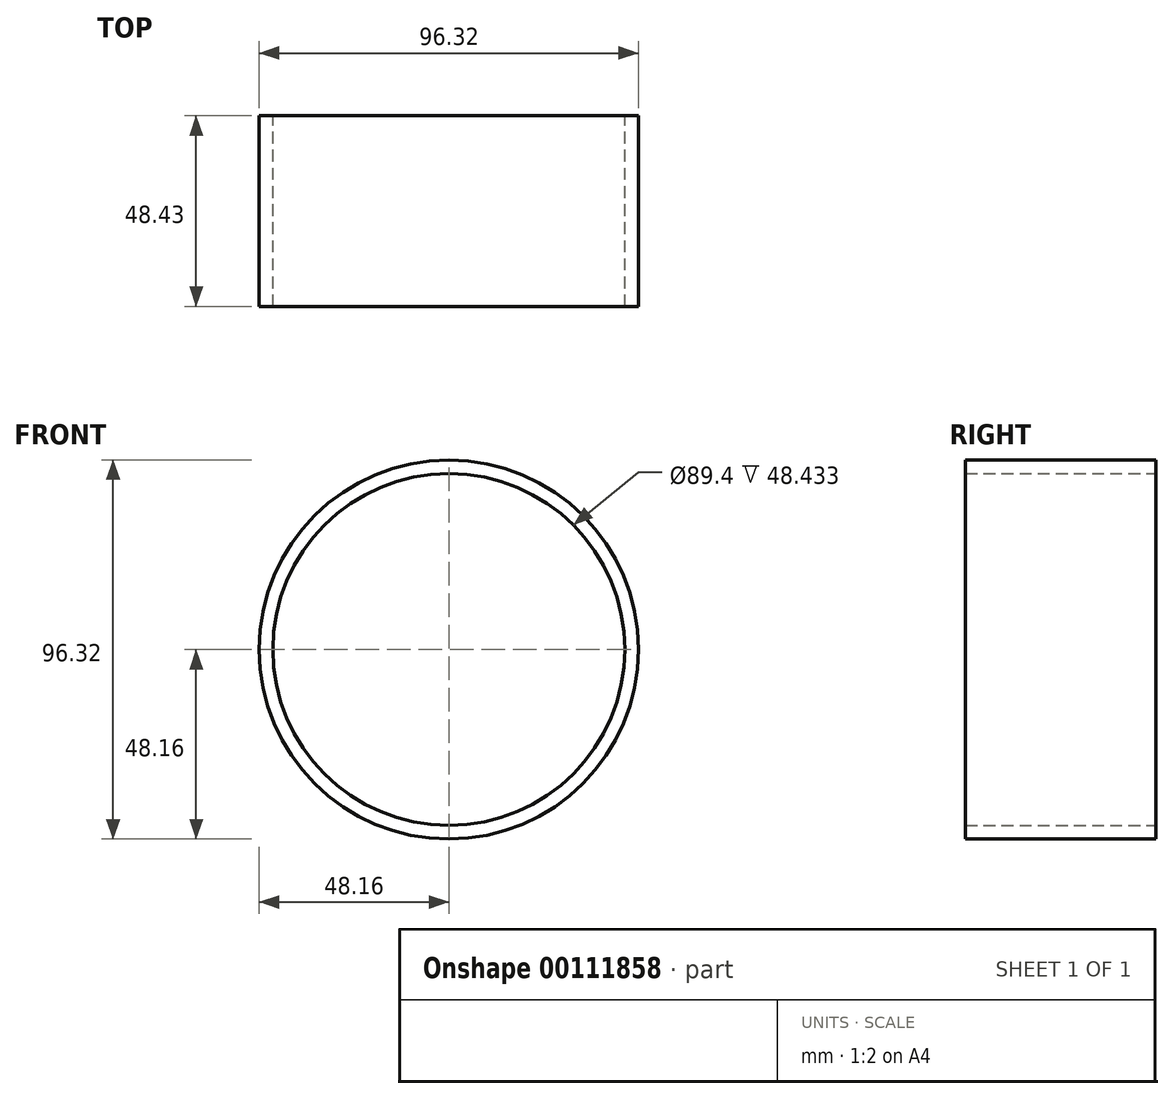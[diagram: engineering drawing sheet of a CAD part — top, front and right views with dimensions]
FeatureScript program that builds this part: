
annotation { "Feature Type Name" : "Feature", "Feature Type Description" : "" }
export const myFeature = defineFeature(function(context is Context, id is Id, definition is map)
    precondition{}
    {
        {
            var Q0;
            Q0=qCreatedBy(makeId("Front.planeOp"),FACE);
            var sketch = newSketch(context, id + "F0", { "sketchPlane" : qUnion([Q0])});
            skCircle(sketch, "E0", {"center": v(0, 0) * mm, "radius": 48.16 * mm});
            skCircle(sketch, "E1", {"center": v(0, 0) * mm, "radius": 44.7 * mm});
            skSolve(sketch);
        }
        {
            var Q0;
            Q0=makeQuery(id+"F0.imprint","IMPRINT",FACE,{"disambiguationData":[TD([[makeQuery(id+"F0.imprint","IMPRINT",EDGE,{"derivedFrom":sQuery(id+"F0.wireOp",EDGE,"E0")}),1.0]])]});
            extrude(context, id + "F1", {"entities" : qUnion([Q0]), "depth" : 48.43 * mm});
        }
    });
